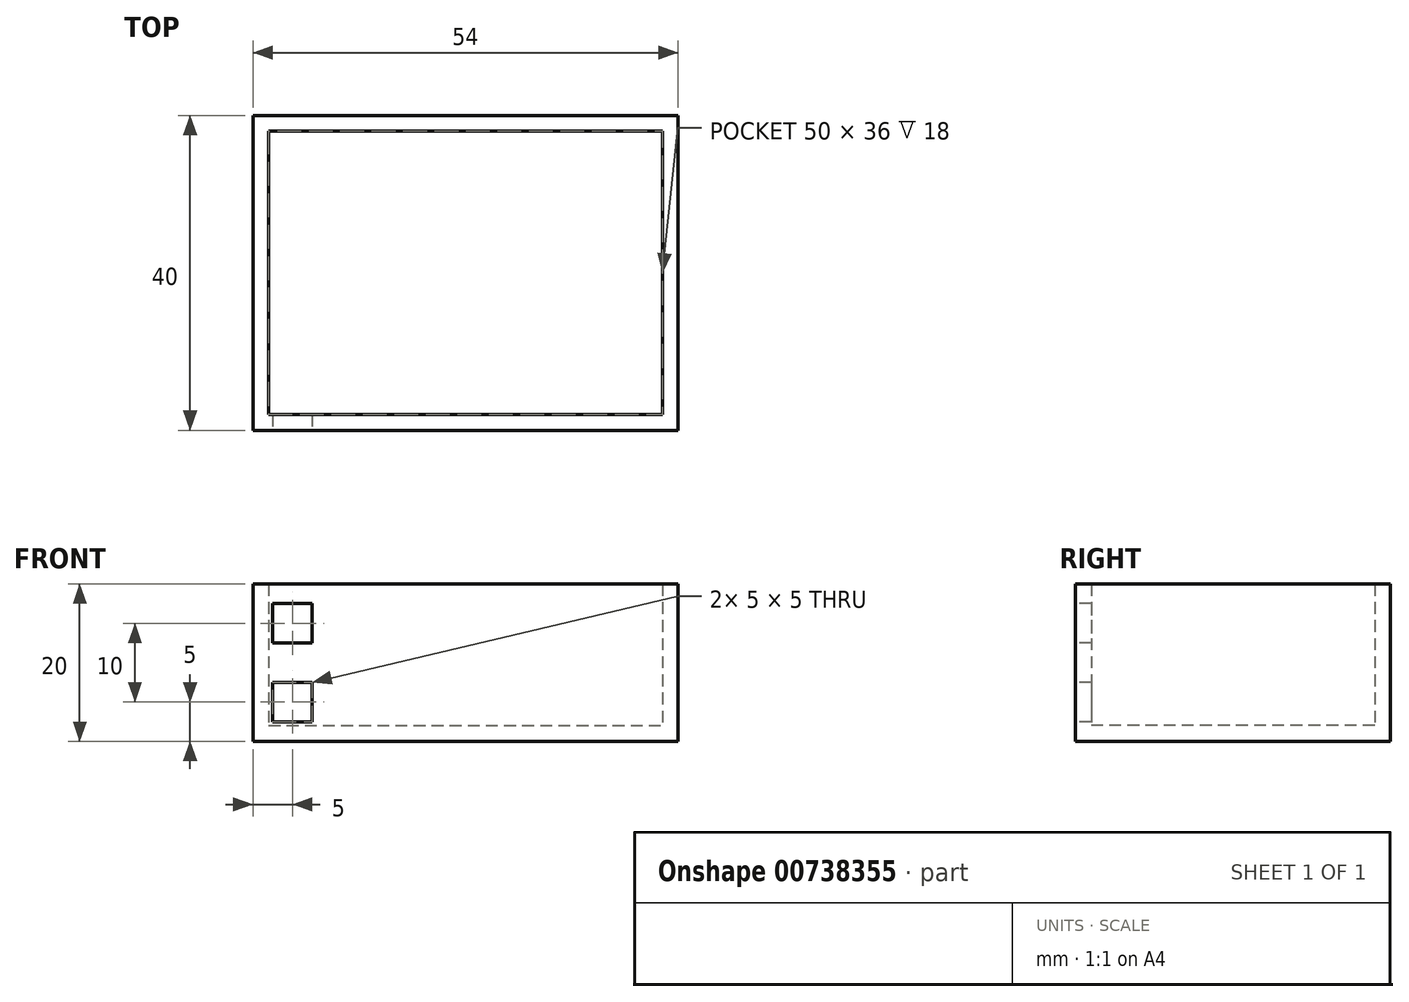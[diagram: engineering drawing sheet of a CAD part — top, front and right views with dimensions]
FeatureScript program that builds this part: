
annotation { "Feature Type Name" : "Feature", "Feature Type Description" : "" }
export const myFeature = defineFeature(function(context is Context, id is Id, definition is map)
    precondition{}
    {
        {
            var Q0;
            Q0=qCreatedBy(makeId("Top.planeOp"),FACE);
            var sketch = newSketch(context, id + "F0", { "sketchPlane" : qUnion([Q0])});
            skLineSegment(sketch, "E0.bottom", {"start": v(-27, 20) * mm, "end": v(27, 20) * mm});
            skLineSegment(sketch, "E0.top", {"start": v(-27, -20) * mm, "end": v(27, -20) * mm});
            skLineSegment(sketch, "E0.left", {"start": v(-27, 20) * mm, "end": v(-27, -20) * mm});
            skLineSegment(sketch, "E0.right", {"start": v(27, 20) * mm, "end": v(27, -20) * mm});
            skPoint(sketch, "E0.middle", {"position": v(0, 0) * mm});
            skSolve(sketch);
        }
        {
            var Q0;
            Q0=makeQuery(id+"F0.imprint","IMPRINT",FACE,{"disambiguationData":[TD([[makeQuery(id+"F0.imprint","IMPRINT",EDGE,{"derivedFrom":sQuery(id+"F0.wireOp",EDGE,"E0.bottom")}),-1.0]])]});
            extrude(context, id + "F1", {"entities" : qUnion([Q0]), "depth" : 20 * mm, "offsetDistance" : 25 * mm});
        }
        {
            var Q0;
            Q0=makeQuery(id+"F1.opExtrude","CAP_FACE",FACE,{"disambiguationData":[OSD([sQuery(id+"F0.wireOp",EDGE,"E0.bottom"),sQuery(id+"F0.wireOp",EDGE,"E0.top"),sQuery(id+"F0.wireOp",EDGE,"E0.left"),sQuery(id+"F0.wireOp",EDGE,"E0.right")])],"isStart":false});
            shell(context, id + "F2", {"entities" : qUnion([Q0]), "thickness" : 2 * mm});
        }
        {
            var Q0;
            Q0=makeQuery(id+"F1.opExtrude","SWEPT_FACE",FACE,{"disambiguationData":[OSD([sQuery(id+"F0.wireOp",EDGE,"E0.top")])]});
            var sketch = newSketch(context, id + "F3", { "sketchPlane" : qUnion([Q0])});
            skLineSegment(sketch, "E1", {"start": v(-24.5, 17.5) * mm, "end": v(-24.5, 12.5) * mm});
            skLineSegment(sketch, "E2", {"start": v(-24.5, 12.5) * mm, "end": v(-19.5, 12.5) * mm});
            skLineSegment(sketch, "E3", {"start": v(-19.5, 12.5) * mm, "end": v(-19.5, 17.5) * mm});
            skLineSegment(sketch, "E4", {"start": v(-19.5, 17.5) * mm, "end": v(-24.5, 17.5) * mm});
            skLineSegment(sketch, "E5", {"start": v(-24.5, 7.5) * mm, "end": v(-24.5, 2.5) * mm});
            skLineSegment(sketch, "E6", {"start": v(-24.5, 2.5) * mm, "end": v(-19.5, 2.5) * mm});
            skLineSegment(sketch, "E7", {"start": v(-19.5, 2.5) * mm, "end": v(-19.5, 7.5) * mm});
            skLineSegment(sketch, "E8", {"start": v(-19.5, 7.5) * mm, "end": v(-24.5, 7.5) * mm});
            skLineSegment(sketch, "E9", {"start": v(-19.9, 20) * mm, "end": v(-19.9, 17.5) * mm, "construction": true});
            skLineSegment(sketch, "E10", {"start": v(-22, 2.5) * mm, "end": v(-22, 0) * mm, "construction": true});
            skSolve(sketch);
        }
        {
            var Q0;
            Q0=makeQuery(id+"F3.imprint","IMPRINT",FACE,{"disambiguationData":[TD([[makeQuery(id+"F3.imprint","IMPRINT",EDGE,{"derivedFrom":sQuery(id+"F3.wireOp",EDGE,"E1")}),1.0]])]});
            var Q1;
            Q1=makeQuery(id+"F3.imprint","IMPRINT",FACE,{"disambiguationData":[TD([[makeQuery(id+"F3.imprint","IMPRINT",EDGE,{"derivedFrom":sQuery(id+"F3.wireOp",EDGE,"E5")}),1.0]])]});
            extrude(context, id + "F4", {"entities" : qUnion([Q0, Q1]), "operationType" : NewBodyOperationType.REMOVE, "oppositeDirection" : true, "depth" : 2 * mm, "offsetDistance" : 25 * mm});
        }
    });
